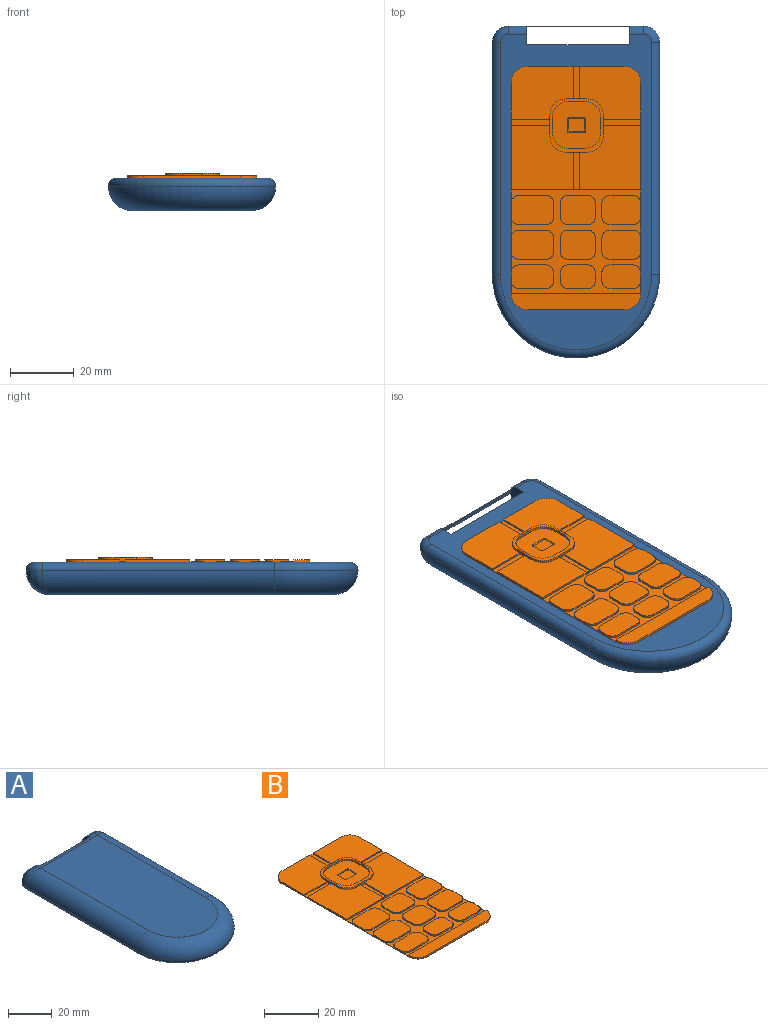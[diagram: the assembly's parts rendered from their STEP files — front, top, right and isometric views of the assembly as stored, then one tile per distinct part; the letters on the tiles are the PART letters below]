
ASSEMBLY  parts=2 mates=1
PART A: 18 faces, bbox 56.6x106.5x10.2 mm
  f0: cylinder r=7.62mm len=42.16mm, axis (1,0,0), area 181.7mm2, adj f1,f2,f5,f8,f14,f15,f16,f17
  f1: cylinder r=2.54mm len=42.16mm, axis (-1,0,0), area 56.2mm2, adj f0,f3,f11,f13,f14,f15,f16
  f2: plane 88.65x37.08mm, normal (0,0,1), area 3139.8mm2, adj f0,f4,f6,f7
  f3: plane 98.81x47.24mm, normal (0,0,-1), area 4317.7mm2, adj f1,f9,f10,f11,f12,f13,f14,f16
  f4: cylinder r=7.62mm len=72.64mm, axis (0,-1,0), area 858.5mm2, adj f2,f5,f6,f9
  f5: bspline ~9.26x7.62mm, area 62.9mm2, adj f0,f4,f11
  f6: torus R=18.54mm, axis (0,0,1), area 879.7mm2, adj f2,f4,f7,f10
  f7: cylinder r=7.62mm len=72.64mm, axis (0,1,0), area 858.5mm2, adj f2,f6,f8,f12
  f8: bspline ~9.26x7.62mm, area 62.9mm2, adj f0,f7,f13
  f9: cylinder r=2.54mm len=72.64mm, axis (0,1,0), area 289.8mm2, adj f3,f4,f10,f11
  f10: torus R=23.62mm, axis (0,0,1), area 316.4mm2, adj f3,f6,f9,f12
  f11: torus R=2.54mm, axis (0,0,1), area 26.1mm2, adj f1,f3,f5,f9
  f12: cylinder r=2.54mm len=72.64mm, axis (0,-1,0), area 289.8mm2, adj f3,f7,f10,f13
  f13: torus R=2.54mm, axis (0,0,1), area 26.1mm2, adj f1,f3,f8,f12
  f14: plane 9.96x5.84mm, normal (1,0,0), area 46.1mm2, adj f0,f1,f3,f15,f17
  f15: plane 32.22x1.4mm, normal (0,-1,0), area 45mm2, adj f0,f1,f14,f16
  f16: plane 9.96x5.84mm, normal (-1,0,0), area 46.1mm2, adj f0,f1,f3,f15,f17
  f17: plane 32.22x9.96mm, normal (0,1,0), area 320.9mm2, adj f0,f3,f14,f16
PART B: 133 faces, bbox 40.6x76.2x1.5 mm
  f0: plane 19.31x16.52mm, normal (0,0,1), area 271.5mm2, adj f1,f6,f19,f93,f96,f108,f119,f125
  f1: plane 30.48x0.76mm, normal (0,1,0), area 22.3mm2, adj f0,f2,f16,f19,f20,f124,f125,f126
  f2: plane 19.42x16.52mm, normal (0,0,1), area 275mm2, adj f1,f3,f20,f93,f94,f105,f122,f124
  f3: plane 66.04x0.76mm, normal (-1,0,0), area 36mm2, adj f2,f7,f8,f9,f10,f16,f17,f20
  f4: plane 15.24x14.73mm, normal (0,0,1), area 176.5mm2, adj f97,f98,f99,f100,f101,f102,f103,f104
  f5: plane 16.68x16.68mm, normal (0,0,1), area 53.9mm2, adj f93,f94,f95,f96,f97,f98,f99,f100
  f6: plane 66.04x0.76mm, normal (1,0,0), area 36mm2, adj f0,f7,f11,f12,f13,f16,f18,f19
  f7: plane 40.64x20.14mm, normal (0,0,1), area 668.1mm2, adj f3,f6,f30,f94,f95,f96,f106,f107
  f8: plane 13.36x9.22mm, normal (0,0,1), area 117.6mm2, adj f3,f31,f32,f33,f57,f58,f71,f74
  f9: plane 13.36x9.22mm, normal (0,0,1), area 117.6mm2, adj f3,f34,f35,f36,f72,f73,f75,f78
  f10: plane 13.36x7.46mm, normal (0,0,1), area 94mm2, adj f3,f37,f38,f39,f76,f77,f87,f88
  f11: plane 12.21x7.46mm, normal (0,0,1), area 85.5mm2, adj f6,f41,f42,f43,f84,f85,f91,f92
  f12: plane 12.21x9.22mm, normal (0,0,1), area 107mm2, adj f6,f44,f45,f46,f64,f65,f83,f86
  f13: plane 12.21x9.22mm, normal (0,0,1), area 107mm2, adj f6,f47,f48,f49,f61,f62,f63,f66
  f14: plane 40.64x5.08mm, normal (0,0,1), area 195.4mm2, adj f15,f17,f18,f40
  f15: plane 30.48x0.76mm, normal (0,-1,0), area 23.2mm2, adj f14,f16,f17,f18
  f16: plane 76.2x40.64mm, normal (0,0,-1), area 3074.6mm2, adj f1,f3,f6,f15,f17,f18,f19,f20
  f17: cylinder r=5.08mm len=5.08mm, axis (0,0,1), area 6.1mm2, adj f3,f14,f15,f16,f40
  f18: cylinder r=5.08mm len=5.08mm, axis (0,0,-1), area 6.1mm2, adj f6,f14,f15,f16,f40
  f19: cylinder r=5.08mm len=5.08mm, axis (0,0,1), area 6.1mm2, adj f0,f1,f6,f16
  f20: cylinder r=5.08mm len=5.08mm, axis (0,0,-1), area 6.1mm2, adj f1,f2,f3,f16
  f21: plane 2.38x0.61mm, normal (-1,0,0), area 1.4mm2, adj f53,f56,f80,f89
  f22: plane 5.98x0.61mm, normal (0,1,0), area 3.6mm2, adj f53,f56,f80,f81
  f23: plane 2.38x0.61mm, normal (1,0,0), area 1.4mm2, adj f53,f56,f81,f90
  f24: plane 4.14x0.61mm, normal (-1,0,0), area 2.5mm2, adj f53,f55,f68,f79
  f25: plane 5.98x0.61mm, normal (0,1,0), area 3.6mm2, adj f53,f55,f68,f69
  f26: plane 4.14x0.61mm, normal (1,0,0), area 2.5mm2, adj f53,f55,f69,f82
  f27: plane 4.14x0.61mm, normal (-1,0,0), area 2.5mm2, adj f53,f54,f59,f67
  f28: plane 5.98x0.61mm, normal (0,1,0), area 3.6mm2, adj f53,f54,f59,f60
  f29: plane 4.14x0.61mm, normal (1,0,0), area 2.5mm2, adj f53,f54,f60,f70
  f30: plane 40.64x0.61mm, normal (0,-1,0), area 24.8mm2, adj f3,f6,f7,f53
  f31: plane 8.28x0.61mm, normal (0,1,0), area 5mm2, adj f8,f53,f57,f58
  f32: plane 4.14x0.61mm, normal (1,0,0), area 2.5mm2, adj f8,f53,f58,f74
  f33: plane 8.28x0.61mm, normal (0,-1,0), area 5mm2, adj f8,f53,f71,f74
  f34: plane 8.28x0.61mm, normal (0,1,0), area 5mm2, adj f9,f53,f72,f73
  f35: plane 4.14x0.61mm, normal (1,0,0), area 2.5mm2, adj f9,f53,f73,f78
  f36: plane 8.28x0.61mm, normal (0,-1,0), area 5mm2, adj f9,f53,f75,f78
  f37: plane 8.28x0.61mm, normal (0,1,0), area 5mm2, adj f10,f53,f76,f77
  f38: plane 2.38x0.61mm, normal (1,0,0), area 1.4mm2, adj f10,f53,f77,f87
  f39: plane 8.28x0.61mm, normal (0,-1,0), area 5mm2, adj f10,f53,f87,f88
  f40: plane 40.64x0.61mm, normal (0,1,0), area 24.8mm2, adj f14,f17,f18,f53
  f41: plane 7.13x0.61mm, normal (0,-1,0), area 4.3mm2, adj f11,f53,f91,f92
  f42: plane 2.38x0.61mm, normal (-1,0,0), area 1.4mm2, adj f11,f53,f84,f91
  f43: plane 7.13x0.61mm, normal (0,1,0), area 4.3mm2, adj f11,f53,f84,f85
  f44: plane 7.13x0.61mm, normal (0,-1,0), area 4.3mm2, adj f12,f53,f83,f86
  f45: plane 4.14x0.61mm, normal (-1,0,0), area 2.5mm2, adj f12,f53,f64,f83
  f46: plane 7.13x0.61mm, normal (0,1,0), area 4.3mm2, adj f12,f53,f64,f65
  f47: plane 7.13x0.61mm, normal (0,-1,0), area 4.3mm2, adj f13,f53,f63,f66
  f48: plane 4.14x0.61mm, normal (-1,0,0), area 2.5mm2, adj f13,f53,f61,f63
  f49: plane 7.13x0.61mm, normal (0,1,0), area 4.3mm2, adj f13,f53,f61,f62
  f50: plane 5.98x0.61mm, normal (0,-1,0), area 3.6mm2, adj f53,f55,f79,f82
  f51: plane 5.98x0.61mm, normal (0,-1,0), area 3.6mm2, adj f53,f54,f67,f70
  f52: plane 5.98x0.61mm, normal (0,-1,0), area 3.6mm2, adj f53,f56,f89,f90
  f53: plane 40.64x32.43mm, normal (0,0,1), area 420mm2, adj f3,f6,f21,f22,f23,f24,f25,f26
  f54: plane 11.06x9.22mm, normal (0,0,1), area 96.4mm2, adj f27,f28,f29,f51,f59,f60,f67,f70
  f55: plane 11.06x9.22mm, normal (0,0,1), area 96.4mm2, adj f24,f25,f26,f50,f68,f69,f79,f82
  f56: plane 11.06x7.46mm, normal (0,0,1), area 76.9mm2, adj f21,f22,f23,f52,f80,f81,f89,f90
  f57: cylinder r=2.54mm len=2.54mm, axis (0,0,-1), area 2.4mm2, adj f3,f8,f31,f53
  f58: cylinder r=2.54mm len=2.54mm, axis (0,0,1), area 2.4mm2, adj f8,f31,f32,f53
  f59: cylinder r=2.54mm len=2.54mm, axis (0,0,1), area 2.4mm2, adj f27,f28,f53,f54
  f60: cylinder r=2.54mm len=2.54mm, axis (0,0,1), area 2.4mm2, adj f28,f29,f53,f54
  f61: cylinder r=2.54mm len=2.54mm, axis (0,0,1), area 2.4mm2, adj f13,f48,f49,f53
  f62: cylinder r=2.54mm len=2.54mm, axis (0,0,1), area 2.4mm2, adj f6,f13,f49,f53
  f63: cylinder r=2.54mm len=2.54mm, axis (0,0,-1), area 2.4mm2, adj f13,f47,f48,f53
  f64: cylinder r=2.54mm len=2.54mm, axis (0,0,1), area 2.4mm2, adj f12,f45,f46,f53
  f65: cylinder r=2.54mm len=2.54mm, axis (0,0,1), area 2.4mm2, adj f6,f12,f46,f53
  f66: cylinder r=2.54mm len=2.54mm, axis (0,0,-1), area 2.4mm2, adj f6,f13,f47,f53
  f67: cylinder r=2.54mm len=2.54mm, axis (0,0,-1), area 2.4mm2, adj f27,f51,f53,f54
  f68: cylinder r=2.54mm len=2.54mm, axis (0,0,1), area 2.4mm2, adj f24,f25,f53,f55
  f69: cylinder r=2.54mm len=2.54mm, axis (0,0,1), area 2.4mm2, adj f25,f26,f53,f55
  f70: cylinder r=2.54mm len=2.54mm, axis (0,0,-1), area 2.4mm2, adj f29,f51,f53,f54
  f71: cylinder r=2.54mm len=2.54mm, axis (0,0,1), area 2.4mm2, adj f3,f8,f33,f53
  f72: cylinder r=2.54mm len=2.54mm, axis (0,0,-1), area 2.4mm2, adj f3,f9,f34,f53
  f73: cylinder r=2.54mm len=2.54mm, axis (0,0,1), area 2.4mm2, adj f9,f34,f35,f53
  f74: cylinder r=2.54mm len=2.54mm, axis (0,0,-1), area 2.4mm2, adj f8,f32,f33,f53
  f75: cylinder r=2.54mm len=2.54mm, axis (0,0,1), area 2.4mm2, adj f3,f9,f36,f53
  f76: cylinder r=2.54mm len=2.54mm, axis (0,0,-1), area 2.4mm2, adj f3,f10,f37,f53
  f77: cylinder r=2.54mm len=2.54mm, axis (0,0,1), area 2.4mm2, adj f10,f37,f38,f53
  f78: cylinder r=2.54mm len=2.54mm, axis (0,0,-1), area 2.4mm2, adj f9,f35,f36,f53
  f79: cylinder r=2.54mm len=2.54mm, axis (0,0,-1), area 2.4mm2, adj f24,f50,f53,f55
  f80: cylinder r=2.54mm len=2.54mm, axis (0,0,1), area 2.4mm2, adj f21,f22,f53,f56
  f81: cylinder r=2.54mm len=2.54mm, axis (0,0,1), area 2.4mm2, adj f22,f23,f53,f56
  f82: cylinder r=2.54mm len=2.54mm, axis (0,0,-1), area 2.4mm2, adj f26,f50,f53,f55
  f83: cylinder r=2.54mm len=2.54mm, axis (0,0,-1), area 2.4mm2, adj f12,f44,f45,f53
  f84: cylinder r=2.54mm len=2.54mm, axis (0,0,1), area 2.4mm2, adj f11,f42,f43,f53
  f85: cylinder r=2.54mm len=2.54mm, axis (0,0,1), area 2.4mm2, adj f6,f11,f43,f53
  f86: cylinder r=2.54mm len=2.54mm, axis (0,0,-1), area 2.4mm2, adj f6,f12,f44,f53
  f87: cylinder r=2.54mm len=2.54mm, axis (0,0,-1), area 2.4mm2, adj f10,f38,f39,f53
  f88: cylinder r=2.54mm len=2.54mm, axis (0,0,1), area 2.4mm2, adj f3,f10,f39,f53
  f89: cylinder r=2.54mm len=2.54mm, axis (0,0,-1), area 2.4mm2, adj f21,f52,f53,f56
  f90: cylinder r=2.54mm len=2.54mm, axis (0,0,-1), area 2.4mm2, adj f23,f52,f53,f56
  f91: cylinder r=2.54mm len=2.54mm, axis (0,0,-1), area 2.4mm2, adj f11,f41,f42,f53
  f92: cylinder r=2.54mm len=2.54mm, axis (0,0,-1), area 2.4mm2, adj f6,f11,f41,f53
  f93: plane 6.52x1.27mm, normal (0,1,0), area 5.9mm2, adj f0,f2,f5,f105,f108,f124,f125,f126
  f94: plane 6.52x1.27mm, normal (-1,0,0), area 6mm2, adj f2,f5,f7,f105,f106,f121,f122,f123
  f95: plane 6.52x0.76mm, normal (0,-1,0), area 5mm2, adj f5,f7,f106,f107,f127
  f96: plane 6.52x1.27mm, normal (1,0,0), area 6mm2, adj f0,f5,f7,f107,f108,f118,f119,f120
  f97: plane 5.08x0.76mm, normal (0,-1,0), area 3.9mm2, adj f4,f5,f101,f104
  f98: plane 4.57x0.76mm, normal (1,0,0), area 3.5mm2, adj f4,f5,f101,f102
  f99: plane 5.08x0.76mm, normal (0,1,0), area 3.9mm2, adj f4,f5,f102,f103
  f100: plane 4.57x0.76mm, normal (-1,0,0), area 3.5mm2, adj f4,f5,f103,f104
  f101: cylinder r=5.08mm len=5.08mm, axis (0,0,1), area 6.1mm2, adj f4,f5,f97,f98
  f102: cylinder r=5.08mm len=5.08mm, axis (0,0,-1), area 6.1mm2, adj f4,f5,f98,f99
  f103: cylinder r=5.08mm len=5.08mm, axis (0,0,1), area 6.1mm2, adj f4,f5,f99,f100
  f104: cylinder r=5.08mm len=5.08mm, axis (0,0,-1), area 6.1mm2, adj f4,f5,f97,f100
  f105: cylinder r=5.08mm len=5.08mm, axis (0,0,1), area 6.1mm2, adj f2,f5,f93,f94
  f106: cylinder r=5.08mm len=5.08mm, axis (0,0,-1), area 6.1mm2, adj f5,f7,f94,f95
  f107: cylinder r=5.08mm len=5.08mm, axis (0,0,1), area 6.1mm2, adj f5,f7,f95,f96
  f108: cylinder r=5.08mm len=5.08mm, axis (0,0,-1), area 6.1mm2, adj f0,f5,f93,f96
  f109: plane 5.19x4.07mm, normal (0,0,1), area 20.9mm2, adj f110,f111,f112,f113,f114,f115,f116,f117
  f110: plane 3.5x0.25mm, normal (-0.71,0,0.71), area 1.2mm2, adj f4,f109,f114,f115
  f111: plane 4.62x0.25mm, normal (0,-0.71,0.71), area 1.6mm2, adj f4,f109,f114,f116
  f112: plane 4.62x0.25mm, normal (0,0.71,0.71), area 1.6mm2, adj f4,f109,f115,f117
  f113: plane 3.5x0.25mm, normal (0.71,0,0.71), area 1.2mm2, adj f4,f109,f116,f117
  f114: cylinder r=0.76mm len=0.88mm, axis (-0.58,-0.58,-0.58), area 0.4mm2, adj f4,f109,f110,f111
  f115: cylinder r=0.76mm len=0.88mm, axis (-0.58,0.58,-0.58), area 0.4mm2, adj f4,f109,f110,f112
  f116: cylinder r=0.76mm len=0.88mm, axis (-0.58,0.58,0.58), area 0.4mm2, adj f4,f109,f111,f113
  f117: cylinder r=0.76mm len=0.88mm, axis (-0.58,-0.58,0.58), area 0.4mm2, adj f4,f109,f112,f113
  f118: plane 11.79x0.51mm, normal (0,1,0), area 6mm2, adj f6,f7,f96,f120
  f119: plane 11.79x0.51mm, normal (0,-1,0), area 6mm2, adj f0,f6,f96,f120
  f120: plane 11.79x2.02mm, normal (0,0,1), area 23.8mm2, adj f6,f96,f118,f119
  f121: plane 12.17x0.51mm, normal (0,1,0), area 6.2mm2, adj f3,f7,f94,f123
  f122: plane 12.17x0.51mm, normal (0,-1,0), area 6.2mm2, adj f2,f3,f94,f123
  f123: plane 12.17x2.02mm, normal (0,0,1), area 24.6mm2, adj f3,f94,f121,f122
  f124: plane 10.2x0.51mm, normal (1,0,0), area 5.2mm2, adj f1,f2,f93,f126
  f125: plane 10.2x0.51mm, normal (-1,0,0), area 5.2mm2, adj f0,f1,f93,f126
  f126: plane 10.2x1.91mm, normal (0,0,1), area 19.5mm2, adj f1,f93,f124,f125
  f127: plane 1.91x0.05mm, normal (0,0,-1), area 0.1mm2, adj f95,f128,f129,f131
  f128: plane 1.91x0.51mm, normal (0,-1,0), area 1mm2, adj f127,f129,f131,f132
  f129: plane 11.74x0.51mm, normal (1,0,0), area 6mm2, adj f7,f127,f128,f130,f132
  f130: plane 1.91x0.51mm, normal (0,1,0), area 1mm2, adj f7,f129,f131,f132
  f131: plane 11.74x0.51mm, normal (-1,0,0), area 6mm2, adj f7,f127,f128,f130,f132
  f132: plane 11.74x1.91mm, normal (0,0,1), area 22.4mm2, adj f128,f129,f130,f131
PLACE A rot(axis=(0,1,0),180deg) t=(37.2,11.72,0)mm
PLACE B t=(-0.03,-1.88,0)mm
MATE fastened A.f3 <-> B.f16  axis (0,0,1) through (49.77,14.9,0)mm
